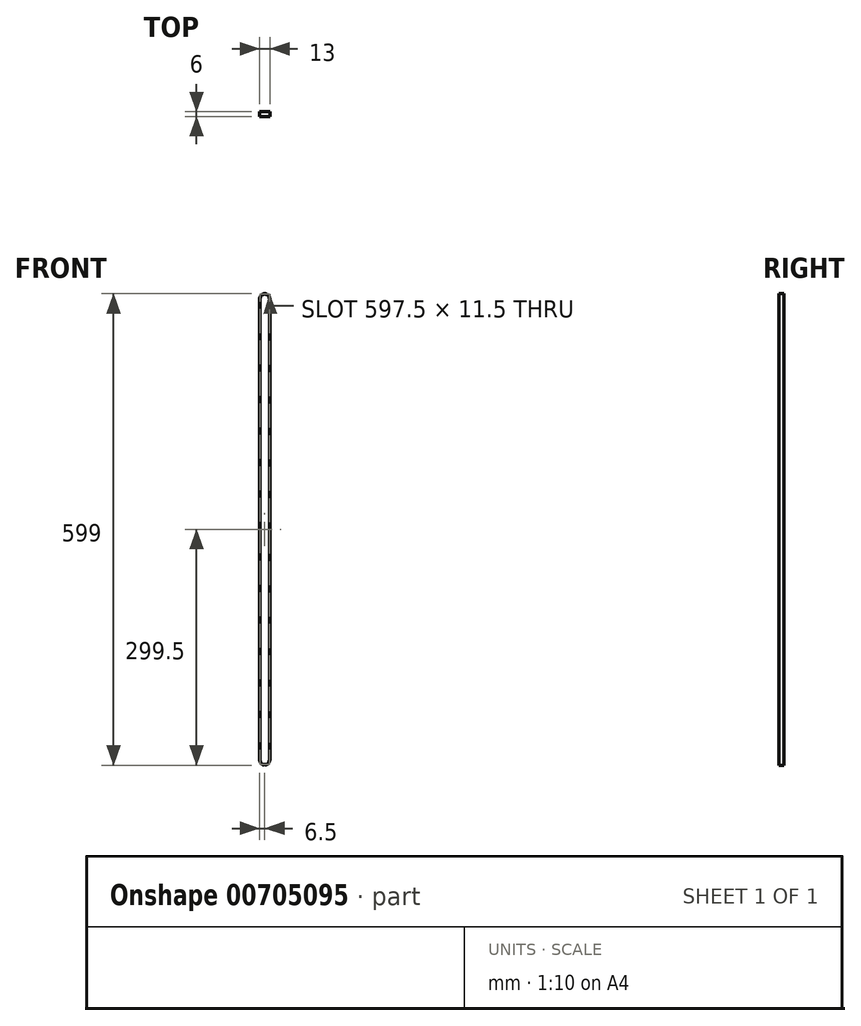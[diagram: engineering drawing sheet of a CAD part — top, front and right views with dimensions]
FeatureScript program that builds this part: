
annotation { "Feature Type Name" : "Feature", "Feature Type Description" : "" }
export const myFeature = defineFeature(function(context is Context, id is Id, definition is map)
    precondition{}
    {
        {
            var Q0;
            Q0=qCreatedBy(makeId("Front.planeOp"),FACE);
            var sketch = newSketch(context, id + "F0", { "sketchPlane" : qUnion([Q0])});
            skPoint(sketch, "E0", {"position": v(0, 0) * mm});
            skPoint(sketch, "E1", {"position": v(0, -586) * mm});
            skArc(sketch, "E2", {"start": v(6.5, 0) * mm, "mid": v(0, 6.5) * mm, "end": v(-6.5, 0) * mm});
            skArc(sketch, "E3", {"start": v(-6.5, -586) * mm, "mid": v(0, -592.5) * mm, "end": v(6.5, -586) * mm});
            skLineSegment(sketch, "E4", {"start": v(-6.5, -586) * mm, "end": v(-6.5, 0) * mm});
            skLineSegment(sketch, "E5", {"start": v(6.5, 0) * mm, "end": v(6.5, -586) * mm});
            skArc(sketch, "E6.0", {"start": v(5.75, 0) * mm, "mid": v(0, 5.75) * mm, "end": v(-5.75, 0) * mm});
            skLineSegment(sketch, "E6.1", {"start": v(5.75, 0) * mm, "end": v(5.75, -586) * mm});
            skArc(sketch, "E6.2", {"start": v(-5.75, -586) * mm, "mid": v(0, -591.75) * mm, "end": v(5.75, -586) * mm});
            skLineSegment(sketch, "E6.3", {"start": v(-5.75, -586) * mm, "end": v(-5.75, 0) * mm});
            skLineSegment(sketch, "E7", {"start": v(-5.75, -5.37) * mm, "end": v(-5, -5.37) * mm});
            skLineSegment(sketch, "E8", {"start": v(-5, -5.37) * mm, "end": v(-5, -6.37) * mm});
            skLineSegment(sketch, "E9", {"start": v(-5, -6.37) * mm, "end": v(-5.75, -6.37) * mm});
            skSolve(sketch);
        }
        {
            var Q0;
            Q0=makeQuery(id+"F0.imprint","IMPRINT",FACE,{"disambiguationData":[TD([[makeQuery(id+"F0.imprint","IMPRINT",EDGE,{"derivedFrom":sQuery(id+"F0.wireOp",EDGE,"E2")}),1.0]])]});
            extrude(context, id + "F1", {"entities" : qUnion([Q0]), "depth" : 6 * mm, "offsetDistance" : 25 * mm});
        }
    });
